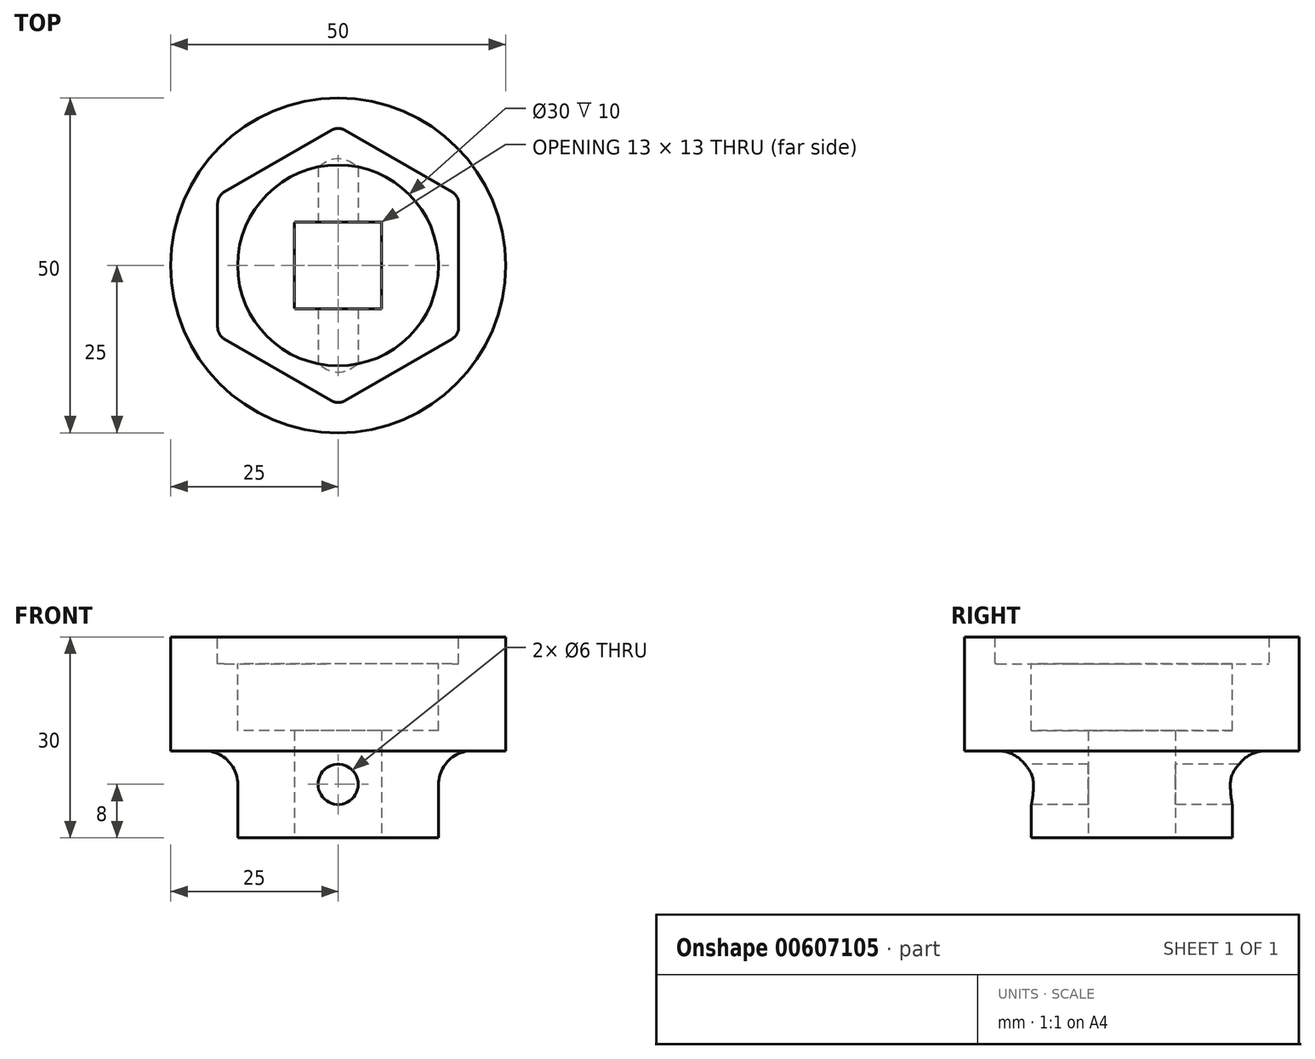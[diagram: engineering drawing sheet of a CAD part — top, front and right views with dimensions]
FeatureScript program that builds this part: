
annotation { "Feature Type Name" : "Feature", "Feature Type Description" : "" }
export const myFeature = defineFeature(function(context is Context, id is Id, definition is map)
    precondition{}
    {
        {
            var Q0;
            Q0=qCreatedBy(makeId("Top.planeOp"),FACE);
            var sketch = newSketch(context, id + "F0", { "sketchPlane" : qUnion([Q0])});
            skCircle(sketch, "E0", {"center": v(0, 0) * mm, "radius": 25 * mm});
            skSolve(sketch);
        }
        {
            var Q0;
            Q0 = qSketchRegion(id + "F0", true);
            extrude(context, id + "F1", {"entities" : qUnion([Q0]), "depth" : 30 * mm, "offsetDistance" : 25 * mm});
        }
        {
            var Q0;
            Q0=makeQuery(id+"F1.opExtrude","CAP_FACE",FACE,{"disambiguationData":[OSD([sQuery(id+"F0.wireOp",EDGE,"E0")])],"isStart":false});
            var sketch = newSketch(context, id + "F2", { "sketchPlane" : qUnion([Q0])});
            skCircle(sketch, "E1.cCircle", {"center": v(0, 0) * mm, "radius": 18 * mm, "construction": true});
            skLineSegment(sketch, "E1.0", {"start": v(0, 20.78) * mm, "end": v(18, 10.4) * mm});
            skLineSegment(sketch, "E1.1", {"start": v(18, 10.4) * mm, "end": v(18, -10.4) * mm});
            skLineSegment(sketch, "E1.2", {"start": v(18, -10.4) * mm, "end": v(0, -20.78) * mm});
            skLineSegment(sketch, "E1.3", {"start": v(0, -20.78) * mm, "end": v(-18, -10.4) * mm});
            skLineSegment(sketch, "E1.4", {"start": v(-18, -10.4) * mm, "end": v(-18, 10.4) * mm});
            skLineSegment(sketch, "E1.5", {"start": v(-18, 10.4) * mm, "end": v(0, 20.78) * mm});
            skPoint(sketch, "E1.0.midPoint", {"position": v(9, 15.59) * mm});
            skCircle(sketch, "E2", {"center": v(0, 20.78) * mm, "radius": 1.5 * mm});
            skCircle(sketch, "E3", {"center": v(18, 10.4) * mm, "radius": 1.5 * mm});
            skCircle(sketch, "E4", {"center": v(18, -10.4) * mm, "radius": 1.5 * mm});
            skCircle(sketch, "E5", {"center": v(0, -20.78) * mm, "radius": 1.5 * mm});
            skCircle(sketch, "E6", {"center": v(-18, -10.4) * mm, "radius": 1.5 * mm});
            skCircle(sketch, "E7", {"center": v(-18, 10.4) * mm, "radius": 1.5 * mm});
            skSolve(sketch);
        }
        {
            var Q0;
            {var subQ6=sQuery(id+"F2.wireOp",EDGE,"E1.0");var subQ12=sQuery(id+"F2.wireOp",EDGE,"E2");var subQ18=makeQuery(id+"F2.imprint","INTERSECT",VERTEX,{"derivedFrom":[subQ6,subQ12]});Q0=makeQuery(id+"F2.imprint","IMPRINT",FACE,{"disambiguationData":[TD([[makeQuery(id+"F2.imprint","IMPRINT",EDGE,{"disambiguationData":[TD([[subQ18,-1.0]])],"derivedFrom":subQ6}),-1.0]])]});}
            var Q1;
            {var subQ0=sQuery(id+"F2.wireOp",EDGE,"E1.5");var subQ1=sQuery(id+"F2.wireOp",EDGE,"E1.4");var subQ2=makeQuery(id+"F2.imprint","INTERSECT",VERTEX,{"derivedFrom":[subQ1,subQ0]});Q1=makeQuery(id+"F2.imprint","IMPRINT",FACE,{"disambiguationData":[TD([[makeQuery(id+"F2.imprint","IMPRINT",EDGE,{"disambiguationData":[TD([[subQ2,1.0]])],"derivedFrom":subQ1}),-1.0]])]});}
            var Q2;
            {var subQ0=sQuery(id+"F2.wireOp",EDGE,"E1.4");var subQ1=sQuery(id+"F2.wireOp",EDGE,"E1.3");var subQ2=makeQuery(id+"F2.imprint","INTERSECT",VERTEX,{"derivedFrom":[subQ1,subQ0]});Q2=makeQuery(id+"F2.imprint","IMPRINT",FACE,{"disambiguationData":[TD([[makeQuery(id+"F2.imprint","IMPRINT",EDGE,{"disambiguationData":[TD([[subQ2,1.0]])],"derivedFrom":subQ1}),-1.0]])]});}
            var Q3;
            {var subQ0=sQuery(id+"F2.wireOp",EDGE,"E1.3");var subQ1=sQuery(id+"F2.wireOp",EDGE,"E1.2");var subQ2=makeQuery(id+"F2.imprint","INTERSECT",VERTEX,{"derivedFrom":[subQ1,subQ0]});Q3=makeQuery(id+"F2.imprint","IMPRINT",FACE,{"disambiguationData":[TD([[makeQuery(id+"F2.imprint","IMPRINT",EDGE,{"disambiguationData":[TD([[subQ2,1.0]])],"derivedFrom":subQ1}),-1.0]])]});}
            var Q4;
            {var subQ0=sQuery(id+"F2.wireOp",EDGE,"E1.2");var subQ1=sQuery(id+"F2.wireOp",EDGE,"E1.1");var subQ2=makeQuery(id+"F2.imprint","INTERSECT",VERTEX,{"derivedFrom":[subQ1,subQ0]});Q4=makeQuery(id+"F2.imprint","IMPRINT",FACE,{"disambiguationData":[TD([[makeQuery(id+"F2.imprint","IMPRINT",EDGE,{"disambiguationData":[TD([[subQ2,1.0]])],"derivedFrom":subQ1}),-1.0]])]});}
            var Q5;
            {var subQ0=sQuery(id+"F2.wireOp",EDGE,"E1.1");var subQ1=sQuery(id+"F2.wireOp",EDGE,"E1.0");var subQ2=makeQuery(id+"F2.imprint","INTERSECT",VERTEX,{"derivedFrom":[subQ1,subQ0]});Q5=makeQuery(id+"F2.imprint","IMPRINT",FACE,{"disambiguationData":[TD([[makeQuery(id+"F2.imprint","IMPRINT",EDGE,{"disambiguationData":[TD([[subQ2,1.0]])],"derivedFrom":subQ1}),-1.0]])]});}
            var Q6;
            {var subQ0=sQuery(id+"F2.wireOp",EDGE,"E1.5");var subQ1=sQuery(id+"F2.wireOp",EDGE,"E1.0");var subQ2=makeQuery(id+"F2.imprint","INTERSECT",VERTEX,{"derivedFrom":[subQ1,subQ0]});Q6=makeQuery(id+"F2.imprint","IMPRINT",FACE,{"disambiguationData":[TD([[makeQuery(id+"F2.imprint","IMPRINT",EDGE,{"disambiguationData":[TD([[subQ2,-1.0]])],"derivedFrom":subQ1}),-1.0]])]});}
            extrude(context, id + "F3", {"entities" : qUnion([Q0, Q1, Q2, Q3, Q4, Q5, Q6]), "operationType" : NewBodyOperationType.REMOVE, "oppositeDirection" : true, "depth" : 4 * mm, "offsetDistance" : 25 * mm});
        }
        {
            var Q0;
            Q0=makeQuery(id+"F1.opExtrude","CAP_FACE",FACE,{"disambiguationData":[OSD([sQuery(id+"F0.wireOp",EDGE,"E0")])],"isStart":false});
            var sketch = newSketch(context, id + "F4", { "sketchPlane" : qUnion([Q0])});
            skCircle(sketch, "E8", {"center": v(0, 0) * mm, "radius": 15 * mm});
            skSolve(sketch);
        }
        {
            var Q0;
            Q0 = qSketchRegion(id + "F4", true);
            extrude(context, id + "F5", {"entities" : qUnion([Q0]), "operationType" : NewBodyOperationType.REMOVE, "oppositeDirection" : true, "depth" : 14 * mm, "offsetDistance" : 25 * mm});
        }
        {
            var Q0;
            Q0=makeQuery(id+"F1.opExtrude","CAP_FACE",FACE,{"disambiguationData":[OSD([sQuery(id+"F0.wireOp",EDGE,"E0")])],"isStart":true});
            var sketch = newSketch(context, id + "F6", { "sketchPlane" : qUnion([Q0])});
            skLineSegment(sketch, "E9.bottom", {"start": v(-6.5, 6.5) * mm, "end": v(6.5, 6.5) * mm});
            skLineSegment(sketch, "E9.top", {"start": v(-6.5, -6.5) * mm, "end": v(6.5, -6.5) * mm});
            skLineSegment(sketch, "E9.left", {"start": v(-6.5, 6.5) * mm, "end": v(-6.5, -6.5) * mm});
            skLineSegment(sketch, "E9.right", {"start": v(6.5, 6.5) * mm, "end": v(6.5, -6.5) * mm});
            skPoint(sketch, "E9.middle", {"position": v(0, 0) * mm});
            skSolve(sketch);
        }
        {
            var Q0;
            Q0 = qSketchRegion(id + "F6", true);
            extrude(context, id + "F7", {"entities" : qUnion([Q0]), "operationType" : NewBodyOperationType.REMOVE, "endBound" : BoundingType.THROUGH_ALL, "oppositeDirection" : true, "depth" : 25 * mm, "offsetDistance" : 25 * mm});
        }
        {
            var Q0;
            Q0=makeQuery(id+"F1.opExtrude","CAP_FACE",FACE,{"disambiguationData":[OSD([sQuery(id+"F0.wireOp",EDGE,"E0")])],"isStart":true});
            var sketch = newSketch(context, id + "F8", { "sketchPlane" : qUnion([Q0])});
            skCircle(sketch, "E10", {"center": v(0, 0) * mm, "radius": 15 * mm});
            skCircle(sketch, "E11.0", {"center": v(0, 0) * mm, "radius": 25 * mm});
            skSolve(sketch);
        }
        {
            var Q0;
            Q0 = qSketchRegion(id + "F8", true);
            extrude(context, id + "F9", {"entities" : qUnion([Q0]), "operationType" : NewBodyOperationType.REMOVE, "oppositeDirection" : true, "depth" : 13 * mm, "offsetDistance" : 25 * mm});
        }
        {
            var Q0;
            Q0=qCreatedBy(makeId("Front.planeOp"),FACE);
            var sketch = newSketch(context, id + "F10", { "sketchPlane" : qUnion([Q0])});
            skCircle(sketch, "E12", {"center": v(0, 8) * mm, "radius": 3 * mm});
            skSolve(sketch);
        }
        {
            var Q0;
            Q0 = qSketchRegion(id + "F10", true);
            extrude(context, id + "F11", {"entities" : qUnion([Q0]), "operationType" : NewBodyOperationType.REMOVE, "endBound" : BoundingType.THROUGH_ALL, "oppositeDirection" : true, "depth" : 25 * mm, "offsetDistance" : 25 * mm, "hasSecondDirection" : true, "secondDirectionBound" : SecondDirectionBoundingType.THROUGH_ALL, "secondDirectionOppositeDirection" : false, "secondDirectionDepth" : 25 * mm});
        }
        {
            var Q0;
            Q0=makeQuery(id+"F9.boolean.opBoolean","COPY",EDGE,{"derivedFrom":makeQuery(id+"F9.opExtrude","CAP_EDGE",EDGE,{"disambiguationData":[OSD([sQuery(id+"F8.wireOp",EDGE,"E10")])],"isStart":false})});
            fillet(context, id + "F12", {"entities" : qUnion([Q0]), "radius" : 5 * mm, "tangentPropagation" : true, "allowEdgeOverflow" : false});
        }
        {
            var Q0;
            Q0=makeQuery(id+"F7.boolean.opBoolean","COPY",EDGE,{"derivedFrom":makeQuery(id+"F7.opExtrude","SWEPT_EDGE",EDGE,{"disambiguationData":[OSD([sQuery(id+"F6.wireOp",EDGE,"E9.bottom"),sQuery(id+"F6.wireOp",EDGE,"E9.left")])]})});
            var Q1;
            Q1=makeQuery(id+"F7.boolean.opBoolean","COPY",EDGE,{"derivedFrom":makeQuery(id+"F7.opExtrude","SWEPT_EDGE",EDGE,{"disambiguationData":[OSD([sQuery(id+"F6.wireOp",EDGE,"E9.top"),sQuery(id+"F6.wireOp",EDGE,"E9.left")])]})});
            var Q2;
            Q2=makeQuery(id+"F7.boolean.opBoolean","COPY",EDGE,{"derivedFrom":makeQuery(id+"F7.opExtrude","SWEPT_EDGE",EDGE,{"disambiguationData":[OSD([sQuery(id+"F6.wireOp",EDGE,"E9.top"),sQuery(id+"F6.wireOp",EDGE,"E9.right")])]})});
            var Q3;
            Q3=makeQuery(id+"F7.boolean.opBoolean","COPY",EDGE,{"derivedFrom":makeQuery(id+"F7.opExtrude","SWEPT_EDGE",EDGE,{"disambiguationData":[OSD([sQuery(id+"F6.wireOp",EDGE,"E9.bottom"),sQuery(id+"F6.wireOp",EDGE,"E9.right")])]})});
            fillet(context, id + "F13", {"entities" : qUnion([Q0, Q1, Q2, Q3]), "radius" : 0.15 * mm, "tangentPropagation" : true, "allowEdgeOverflow" : false});
        }
        {
            var Q0;
            Q0=makeQuery(id+"F3.boolean.opBoolean","COPY",EDGE,{"derivedFrom":makeQuery(id+"F3.opExtrude","SWEPT_EDGE",EDGE,{"disambiguationData":[OSD([sQuery(id+"F2.wireOp",EDGE,"E1.3"),sQuery(id+"F2.wireOp",EDGE,"E1.4")])]})});
            var Q1;
            Q1=makeQuery(id+"F3.boolean.opBoolean","COPY",EDGE,{"derivedFrom":makeQuery(id+"F3.opExtrude","SWEPT_EDGE",EDGE,{"disambiguationData":[OSD([sQuery(id+"F2.wireOp",EDGE,"E1.4"),sQuery(id+"F2.wireOp",EDGE,"E1.5")])]})});
            var Q2;
            Q2=makeQuery(id+"F3.boolean.opBoolean","COPY",EDGE,{"derivedFrom":makeQuery(id+"F3.opExtrude","SWEPT_EDGE",EDGE,{"disambiguationData":[OSD([sQuery(id+"F2.wireOp",EDGE,"E1.2"),sQuery(id+"F2.wireOp",EDGE,"E1.3")])]})});
            var Q3;
            Q3=makeQuery(id+"F3.boolean.opBoolean","COPY",EDGE,{"derivedFrom":makeQuery(id+"F3.opExtrude","SWEPT_EDGE",EDGE,{"disambiguationData":[OSD([sQuery(id+"F2.wireOp",EDGE,"E1.1"),sQuery(id+"F2.wireOp",EDGE,"E1.2")])]})});
            var Q4;
            Q4=makeQuery(id+"F3.boolean.opBoolean","COPY",EDGE,{"derivedFrom":makeQuery(id+"F3.opExtrude","SWEPT_EDGE",EDGE,{"disambiguationData":[OSD([sQuery(id+"F2.wireOp",EDGE,"E1.0"),sQuery(id+"F2.wireOp",EDGE,"E1.1")])]})});
            var Q5;
            Q5=makeQuery(id+"F3.boolean.opBoolean","COPY",EDGE,{"derivedFrom":makeQuery(id+"F3.opExtrude","SWEPT_EDGE",EDGE,{"disambiguationData":[OSD([sQuery(id+"F2.wireOp",EDGE,"E1.0"),sQuery(id+"F2.wireOp",EDGE,"E1.5")])]})});
            fillet(context, id + "F14", {"entities" : qUnion([Q0, Q1, Q2, Q3, Q4, Q5]), "radius" : 2 * mm, "tangentPropagation" : true, "allowEdgeOverflow" : false});
        }
    });
